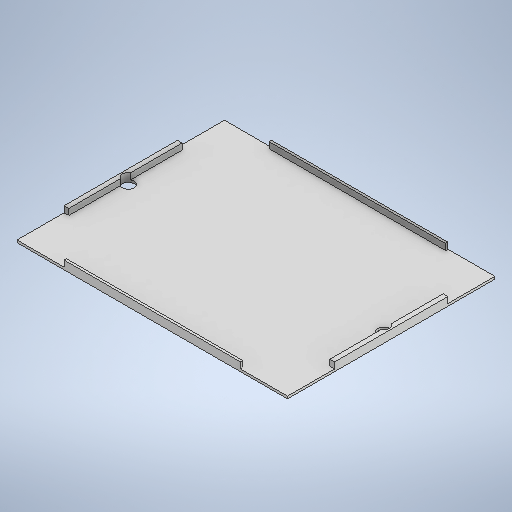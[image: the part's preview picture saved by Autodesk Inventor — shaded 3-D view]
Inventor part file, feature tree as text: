
AUTODESK INVENTOR PART (.ipt)
format: ipt  version: 2025 (Build 290162000, 162)  size: 283,136 bytes
history: native  units: mm
features: sketch x5, extrude x4, hole x1
ambient origin geometry x8: Origin, YZ Plane, XZ Plane, XY Plane, X Axis, Y Axis, Z Axis, Center Point
bodies: Solid1 (feature_tree)
feature tree (10):
  extrude  "Extrusion1"  Depth=44.1mm
  extrude  "Extrusion2"  Depth=1.0mm
  hole  "Hole1"  [1 undecoded]
  extrude  "Extrusion3"  Depth=1.6mm
  extrude  "Extrusion4"  Depth=0.5mm
  sketch  "Sketch1"  dims[d0=0.5mm d1=0.0mm d2=44.1mm]
  sketch  "Sketch2"  dims[d3=57.5mm d4=1.0mm]
  sketch  "Sketch3"  dims[d5=1.0mm d6=1.3mm d7=0.0mm]
  sketch  "Sketch4"  dims[d8=1.6mm d9=1.6mm]
  sketch  "Sketch5"  dims[d10=2.5mm d11=4.0mm d12=4.0mm d13=2.0mm d14=90.0deg d15=6.3mm d16=20.594885mm d17=0.5mm d18=0.5mm d19=1.3mm d20=0.0mm d21=10.0mm d22=10.0mm d23=10.0mm d24=10.0mm d25=10.0mm d26=10.0mm d27=10.0mm d28=10.0mm d29=10.0mm d30=0.0mm]
note: 1 required parameter value undecoded (feature->parameter linkage not recoverable at this tier; creation-order binding heuristic only, values carry confidence <= 0.55)
